# Revit family: BAS-IP_Вызывная панель_AA-14FBIS
name_source: partatom
category: Устройства связи
units: mm (PartAtom-declared; Revit-internal decimal feet)

## family parameters
Всегда вертикально = Да
На основе рабочей плоскости = Нет
Общий = Нет
При загрузке вырезать с полостями = Нет
Размер круглого соединителя = Использовать диаметр
Сохранять ориентацию аннотаций = Нет
Тип детали = Нормальный
Точка расчета площади = Нет

## types (2) — shared parameters
ADSK_Единица измерения = шт.
ADSK_Завод-изготовитель = BAS-IP
ADSK_Количество = 1
ADSK_Наименование = Многоабонентская IP вызывная панель
IK-код = IK06
Выходное видео = Full HD (1920 × 1080), H.264 Main Profile
Дисплей = 10.1" IPS экран с подсветкой и подогревом
Изготовитель = BAS-IP
Камера = 1/3”
Класс степени защиты = IP65
Корпус = Алюминий
Минимальная освещенность = 0,01 Люкс
Ночная подсветка = 6 светодиодов
Питание = PoE IEEE802.3at, +12 В постоянного тока
Потребление питания = 17,8 Вт, в режиме ожидания - 3,8 Вт
Размер под установку = 172 × 379 × 58 мм
Размер самой панели = 180 × 400 × 45 мм
Разрешение = 2 Мп
Температурный режим = -40 – +65 °С
Тип клавиатуры = Сенсорная
Тип панели = Многоабонентская
Тип установки = Скрытого мотажа, накладной с BR-AA14
Угол обзора камеры = 110° (по горизонтали)

## per-type parameters (varying)
| type | ADSK_Марка | ADSK_Материал | Цвет |
| Серебристый | AA-14FBIS Silver | Silver | Gray silver |
| Черный | AA-14FBIS Black | Black silver | Black silver 2 |

note: column(s) folded — value = type name in every type: Цветовое решение
